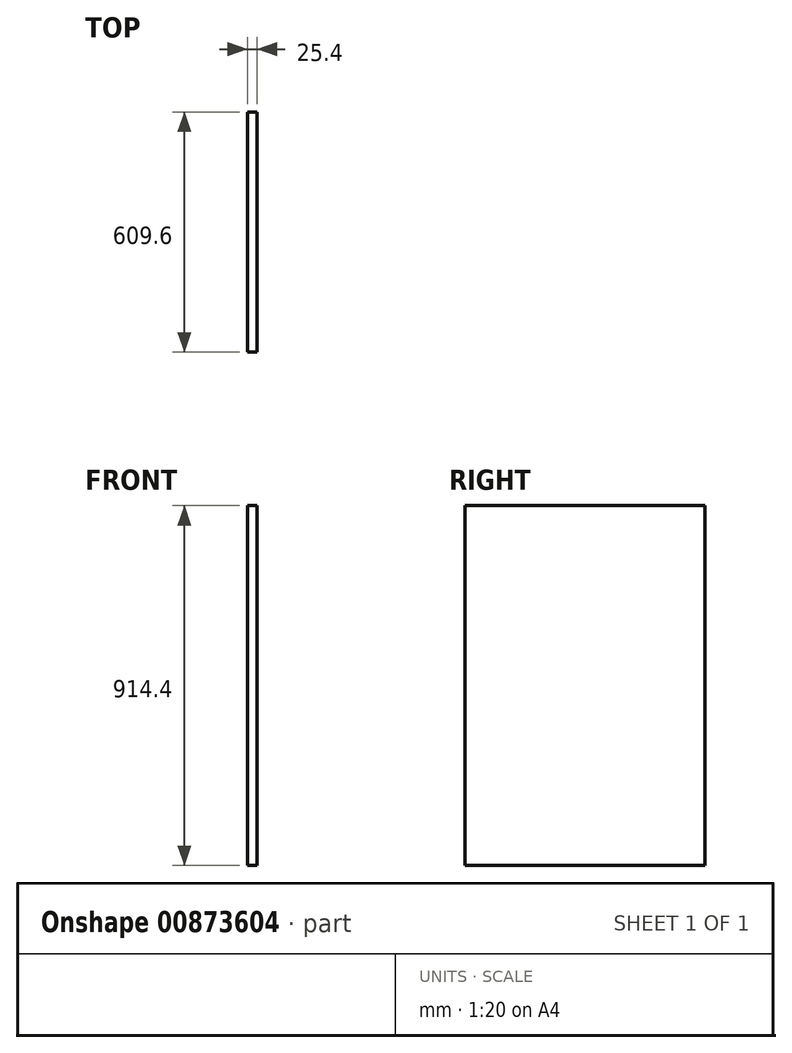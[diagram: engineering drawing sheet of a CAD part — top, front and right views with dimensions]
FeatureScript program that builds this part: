
annotation { "Feature Type Name" : "Feature", "Feature Type Description" : "" }
export const myFeature = defineFeature(function(context is Context, id is Id, definition is map)
    precondition{}
    {
        {
            var Q0;
            Q0=qCreatedBy(makeId("Top.planeOp"),FACE);
            var sketch = newSketch(context, id + "F0", { "sketchPlane" : qUnion([Q0])});
            skLineSegment(sketch, "E0.bottom", {"start": v(0, 0) * mm, "end": v(25.4, 0) * mm});
            skLineSegment(sketch, "E0.top", {"start": v(0, 609.6) * mm, "end": v(25.4, 609.6) * mm});
            skLineSegment(sketch, "E0.left", {"start": v(0, 0) * mm, "end": v(0, 609.6) * mm});
            skLineSegment(sketch, "E0.right", {"start": v(25.4, 0) * mm, "end": v(25.4, 609.6) * mm});
            skLineSegment(sketch, "E1", {"start": v(-23.54, 304.8) * mm, "end": v(125.16, 304.8) * mm, "construction": true});
            skPoint(sketch, "E1.startSnap0", {"position": v(0, 304.8) * mm});
            skLineSegment(sketch, "E2.bottom", {"start": v(25.4, 609.6) * mm, "end": v(50.8, 609.6) * mm, "construction": true});
            skLineSegment(sketch, "E2.top", {"start": v(25.4, 558.8) * mm, "end": v(50.8, 558.8) * mm, "construction": true});
            skLineSegment(sketch, "E2.left", {"start": v(25.4, 609.6) * mm, "end": v(25.4, 558.8) * mm});
            skLineSegment(sketch, "E2.right", {"start": v(50.8, 609.6) * mm, "end": v(50.8, 558.8) * mm, "construction": true});
            skSolve(sketch);
        }
        {
            var Q0;
            Q0 = qSketchRegion(id + "F0", true);
            extrude(context, id + "F1", {"entities" : qUnion([Q0]), "oppositeDirection" : true, "depth" : 914.4 * mm, "offsetDistance" : 25.4 * mm});
        }
    });
